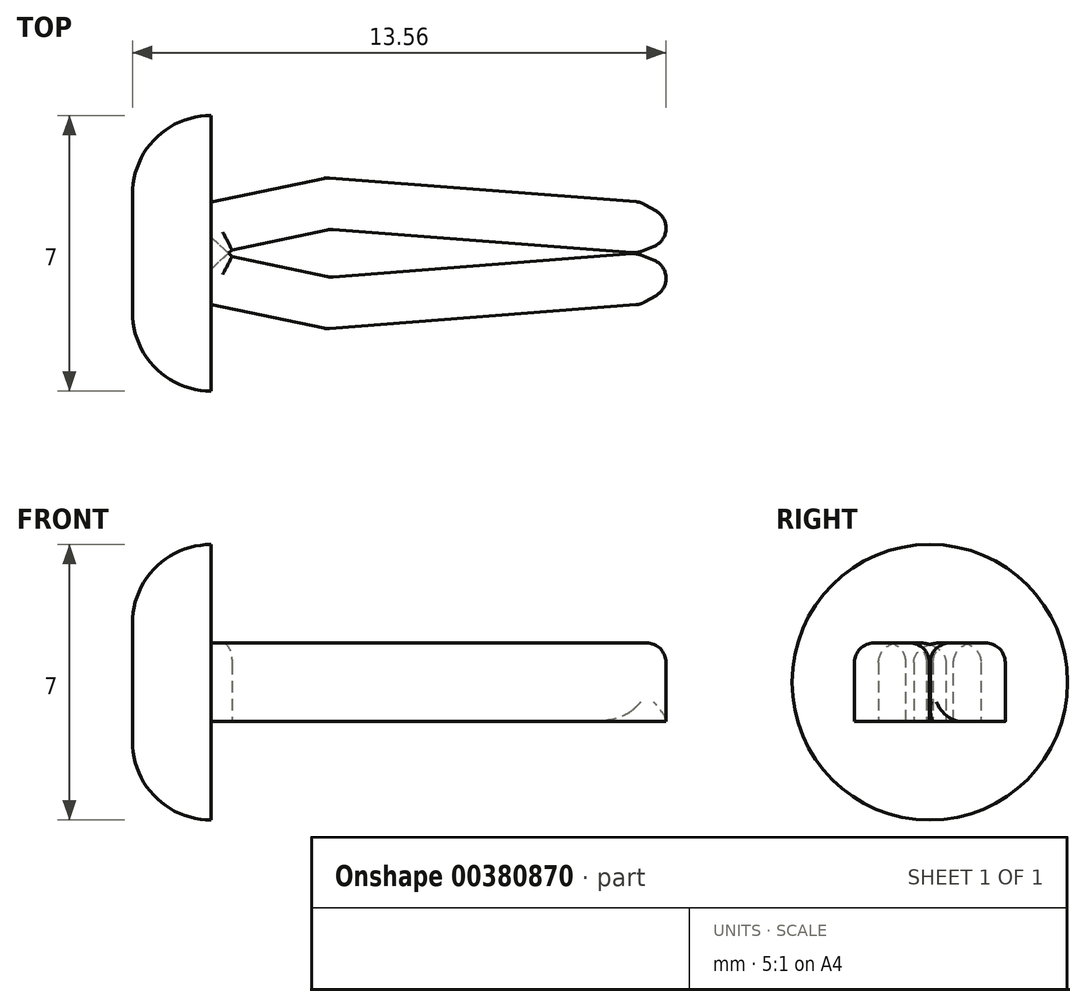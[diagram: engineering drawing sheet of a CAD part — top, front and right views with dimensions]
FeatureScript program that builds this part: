
annotation { "Feature Type Name" : "Feature", "Feature Type Description" : "" }
export const myFeature = defineFeature(function(context is Context, id is Id, definition is map)
    precondition{}
    {
        {
            var Q0;
            Q0=qCreatedBy(makeId("Top.planeOp"),FACE);
            var sketch = newSketch(context, id + "F0", { "sketchPlane" : qUnion([Q0])});
            skLineSegment(sketch, "E0", {"start": v(0, 0) * mm, "end": v(2.94, 0.62) * mm});
            skLineSegment(sketch, "E1", {"start": v(2.94, 0.62) * mm, "end": v(10.91, 0) * mm});
            skLineSegment(sketch, "E2.0", {"start": v(3.02, -0.7) * mm, "end": v(10.81, -1.3) * mm});
            skLineSegment(sketch, "E2.1", {"start": v(0.53, -1.22) * mm, "end": v(3.02, -0.7) * mm});
            skLineSegment(sketch, "E3", {"start": v(10.81, -1.3) * mm, "end": v(12.2, -0.75) * mm});
            skLineSegment(sketch, "E4", {"start": v(12.2, -0.75) * mm, "end": v(10.91, 0) * mm});
            skLineSegment(sketch, "E5", {"start": v(0.53, -1.22) * mm, "end": v(0, -1.7) * mm});
            skLineSegment(sketch, "E6", {"start": v(0, -1.7) * mm, "end": v(0, 0) * mm});
            skSolve(sketch);
        }
        {
            var Q0;
            Q0=makeQuery(id+"F0.imprint","IMPRINT",FACE,{"disambiguationData":[TD([[makeQuery(id+"F0.imprint","IMPRINT",EDGE,{"derivedFrom":sQuery(id+"F0.wireOp",EDGE,"E0")}),-1.0]])]});
            extrude(context, id + "F1", {"entities" : qUnion([Q0]), "depth" : 2 * mm});
        }
        {
            var Q0;
            Q0=qCreatedBy(makeId("Front.planeOp"),FACE);
            cPlane(context, id + "F2", {"entities" : qUnion([Q0]), "cplaneType" : CPlaneType.OFFSET, "offset" : 1.3 * mm, "width" : 150 * mm, "height" : 150 * mm});
        }
        {
            var Q0;
            Q0=makeQuery(id+"F1.opExtrude","SWEPT_BODY",BODY,{"disambiguationData":[OSD([sQuery(id+"F0.wireOp",EDGE,"E0"),sQuery(id+"F0.wireOp",EDGE,"E1"),sQuery(id+"F0.wireOp",EDGE,"E2.0"),sQuery(id+"F0.wireOp",EDGE,"E2.1"),sQuery(id+"F0.wireOp",EDGE,"E3"),sQuery(id+"F0.wireOp",EDGE,"E4"),sQuery(id+"F0.wireOp",EDGE,"E5"),sQuery(id+"F0.wireOp",EDGE,"E6")])]});
            var Q1;
            Q1=qCreatedBy(id+"F2.planeOp",FACE);
            mirror(context, id + "F3", {"entities" : qUnion([Q0]), "mirrorPlane" : qUnion([Q1])});
        }
        {
            var Q0;
            Q0=makeQuery(id+"F1.opExtrude","CAP_EDGE",EDGE,{"disambiguationData":[OSD([sQuery(id+"F0.wireOp",EDGE,"E2.0")])],"isStart":false});
            var Q1;
            Q1=makeQuery(id+"F1.opExtrude","CAP_EDGE",EDGE,{"disambiguationData":[OSD([sQuery(id+"F0.wireOp",EDGE,"E1")])],"isStart":false});
            var Q2;
            Q2=makeQuery(id+"F1.opExtrude","CAP_EDGE",EDGE,{"disambiguationData":[OSD([sQuery(id+"F0.wireOp",EDGE,"E4")])],"isStart":false});
            var Q3;
            Q3=makeQuery(id+"F1.opExtrude","SWEPT_FACE",FACE,{"disambiguationData":[OSD([sQuery(id+"F0.wireOp",EDGE,"E3")])]});
            var Q4;
            Q4=makeQuery(id+"F1.opExtrude","CAP_EDGE",EDGE,{"disambiguationData":[OSD([sQuery(id+"F0.wireOp",EDGE,"E0")])],"isStart":false});
            var Q5;
            Q5=makeQuery(id+"F1.opExtrude","CAP_EDGE",EDGE,{"disambiguationData":[OSD([sQuery(id+"F0.wireOp",EDGE,"E2.1")])],"isStart":false});
            var Q6;
            Q6=makeQuery(id+"F1.opExtrude","SWEPT_EDGE",EDGE,{"disambiguationData":[OSD([sQuery(id+"F0.wireOp",EDGE,"E2.0"),sQuery(id+"F0.wireOp",EDGE,"E2.1")])]});
            var Q7;
            Q7=makeQuery(id+"F3.opPattern","COPY",EDGE,{"derivedFrom":makeQuery(id+"F1.opExtrude","SWEPT_EDGE",EDGE,{"disambiguationData":[OSD([sQuery(id+"F0.wireOp",EDGE,"E2.0"),sQuery(id+"F0.wireOp",EDGE,"E2.1")])]}),"instanceName":"1"});
            var Q8;
            Q8=makeQuery(id+"F3.opPattern","COPY",EDGE,{"derivedFrom":makeQuery(id+"F1.opExtrude","SWEPT_EDGE",EDGE,{"disambiguationData":[OSD([sQuery(id+"F0.wireOp",EDGE,"E2.0"),sQuery(id+"F0.wireOp",EDGE,"E3")])]}),"instanceName":"1"});
            var Q9;
            Q9=makeQuery(id+"F3.opPattern","COPY",EDGE,{"derivedFrom":makeQuery(id+"F1.opExtrude","SWEPT_EDGE",EDGE,{"disambiguationData":[OSD([sQuery(id+"F0.wireOp",EDGE,"E3"),sQuery(id+"F0.wireOp",EDGE,"E4")])]}),"instanceName":"1"});
            var Q10;
            Q10=makeQuery(id+"F3.opPattern","COPY",EDGE,{"derivedFrom":makeQuery(id+"F1.opExtrude","SWEPT_EDGE",EDGE,{"disambiguationData":[OSD([sQuery(id+"F0.wireOp",EDGE,"E1"),sQuery(id+"F0.wireOp",EDGE,"E4")])]}),"instanceName":"1"});
            var Q11;
            Q11=makeQuery(id+"F3.opPattern","COPY",EDGE,{"derivedFrom":makeQuery(id+"F1.opExtrude","CAP_EDGE",EDGE,{"disambiguationData":[OSD([sQuery(id+"F0.wireOp",EDGE,"E1")])],"isStart":false}),"instanceName":"1"});
            var Q12;
            Q12=makeQuery(id+"F3.opPattern","COPY",EDGE,{"derivedFrom":makeQuery(id+"F1.opExtrude","CAP_EDGE",EDGE,{"disambiguationData":[OSD([sQuery(id+"F0.wireOp",EDGE,"E4")])],"isStart":false}),"instanceName":"1"});
            var Q13;
            Q13=makeQuery(id+"F3.opPattern","COPY",EDGE,{"derivedFrom":makeQuery(id+"F1.opExtrude","CAP_EDGE",EDGE,{"disambiguationData":[OSD([sQuery(id+"F0.wireOp",EDGE,"E2.0")])],"isStart":false}),"instanceName":"1"});
            var Q14;
            Q14=makeQuery(id+"F3.opPattern","COPY",EDGE,{"derivedFrom":makeQuery(id+"F1.opExtrude","CAP_EDGE",EDGE,{"disambiguationData":[OSD([sQuery(id+"F0.wireOp",EDGE,"E3")])],"isStart":false}),"instanceName":"1"});
            var Q15;
            Q15=makeQuery(id+"F3.opPattern","COPY",EDGE,{"derivedFrom":makeQuery(id+"F1.opExtrude","CAP_EDGE",EDGE,{"disambiguationData":[OSD([sQuery(id+"F0.wireOp",EDGE,"E0")])],"isStart":false}),"instanceName":"1"});
            var Q16;
            Q16=makeQuery(id+"F3.opPattern","COPY",EDGE,{"derivedFrom":makeQuery(id+"F1.opExtrude","SWEPT_EDGE",EDGE,{"disambiguationData":[OSD([sQuery(id+"F0.wireOp",EDGE,"E0"),sQuery(id+"F0.wireOp",EDGE,"E1")])]}),"instanceName":"1"});
            var Q17;
            Q17=makeQuery(id+"F3.opPattern","COPY",EDGE,{"derivedFrom":makeQuery(id+"F1.opExtrude","CAP_EDGE",EDGE,{"disambiguationData":[OSD([sQuery(id+"F0.wireOp",EDGE,"E2.1")])],"isStart":false}),"instanceName":"1"});
            var Q18;
            Q18=makeQuery(id+"F3.opPattern","COPY",EDGE,{"derivedFrom":makeQuery(id+"F1.opExtrude","CAP_EDGE",EDGE,{"disambiguationData":[OSD([sQuery(id+"F0.wireOp",EDGE,"E5")])],"isStart":false}),"instanceName":"1"});
            var Q19;
            Q19=makeQuery(id+"F1.opExtrude","CAP_EDGE",EDGE,{"disambiguationData":[OSD([sQuery(id+"F0.wireOp",EDGE,"E5")])],"isStart":false});
            var Q20;
            Q20=makeQuery(id+"F1.opExtrude","SWEPT_EDGE",EDGE,{"disambiguationData":[OSD([sQuery(id+"F0.wireOp",EDGE,"E1"),sQuery(id+"F0.wireOp",EDGE,"E4")])]});
            var Q21;
            Q21=makeQuery(id+"F1.opExtrude","SWEPT_EDGE",EDGE,{"disambiguationData":[OSD([sQuery(id+"F0.wireOp",EDGE,"E0"),sQuery(id+"F0.wireOp",EDGE,"E1")])]});
            fillet(context, id + "F4", {"entities" : qUnion([Q0, Q1, Q2, Q3, Q4, Q5, Q6, Q7, Q8, Q9, Q10, Q11, Q12, Q13, Q14, Q15, Q16, Q17, Q18, Q19, Q20, Q21]), "radius" : 0.5 * mm, "tangentPropagation" : true, "allowEdgeOverflow" : false});
        }
        {
            var Q0;
            Q0=makeQuery(id+"F1.opExtrude","SWEPT_FACE",FACE,{"disambiguationData":[OSD([sQuery(id+"F0.wireOp",EDGE,"E6")])]});
            var sketch = newSketch(context, id + "F5", { "sketchPlane" : qUnion([Q0])});
            skPoint(sketch, "E7", {"position": v(1.3, 0) * mm});
            skCircle(sketch, "E8", {"center": v(1.3, 1) * mm, "radius": 3.5 * mm});
            skPoint(sketch, "E9", {"position": v(1.3, 1.96) * mm});
            skSolve(sketch);
        }
        {
            var Q0;
            Q0=makeQuery(id+"F5.imprint","IMPRINT",FACE,{"disambiguationData":[TD([[makeQuery(id+"F5.imprint","IMPRINT",EDGE,{"derivedFrom":sQuery(id+"F5.wireOp",EDGE,"E8")}),1.0]])]});
            var Q1;
            {var subQ0=sQuery(id+"F0.wireOp",EDGE,"E6");Q1=makeQuery(id+"F5.imprint","IMPRINT",FACE,{"disambiguationData":[TD([[makeQuery(id+"F5.imprint","IMPRINT",EDGE,{"derivedFrom":makeQuery(id+"F1.opExtrude","CAP_EDGE",EDGE,{"disambiguationData":[OSD([subQ0])],"isStart":true})}),-1.0]])]});}
            extrude(context, id + "F6", {"entities" : qUnion([Q0, Q1]), "depth" : 2 * mm});
        }
        {
            var Q0;
            Q0=makeQuery(id+"F6.opExtrude","CAP_EDGE",EDGE,{"disambiguationData":[OSD([sQuery(id+"F5.wireOp",EDGE,"E8")])],"isStart":false});
            fillet(context, id + "F7", {"entities" : qUnion([Q0]), "radius" : 2 * mm, "tangentPropagation" : true, "allowEdgeOverflow" : false});
        }
    });
